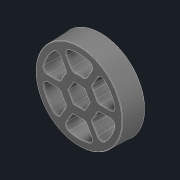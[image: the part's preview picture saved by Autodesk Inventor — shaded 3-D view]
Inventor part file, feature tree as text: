
AUTODESK INVENTOR PART (.ipt)
format: ipt  version: 2021 (Build 250183000, 183)  size: 747,520 bytes
history: native  units: in
note: dims shown in document units (in); Inventor stores cm internally (conversion verified against a paired STEP export)
features: fillet x1
ambient origin geometry x8: Origin, YZ Plane, XZ Plane, XY Plane, X Axis, Y Axis, Z Axis, Center Point
bodies: Solid1 (feature_tree)
feature tree (1):
  fillet  "Fillet3"  [1 undecoded]
note: 1 required parameter value undecoded (feature->parameter linkage not recoverable at this tier; creation-order binding heuristic only, values carry confidence <= 0.55)
